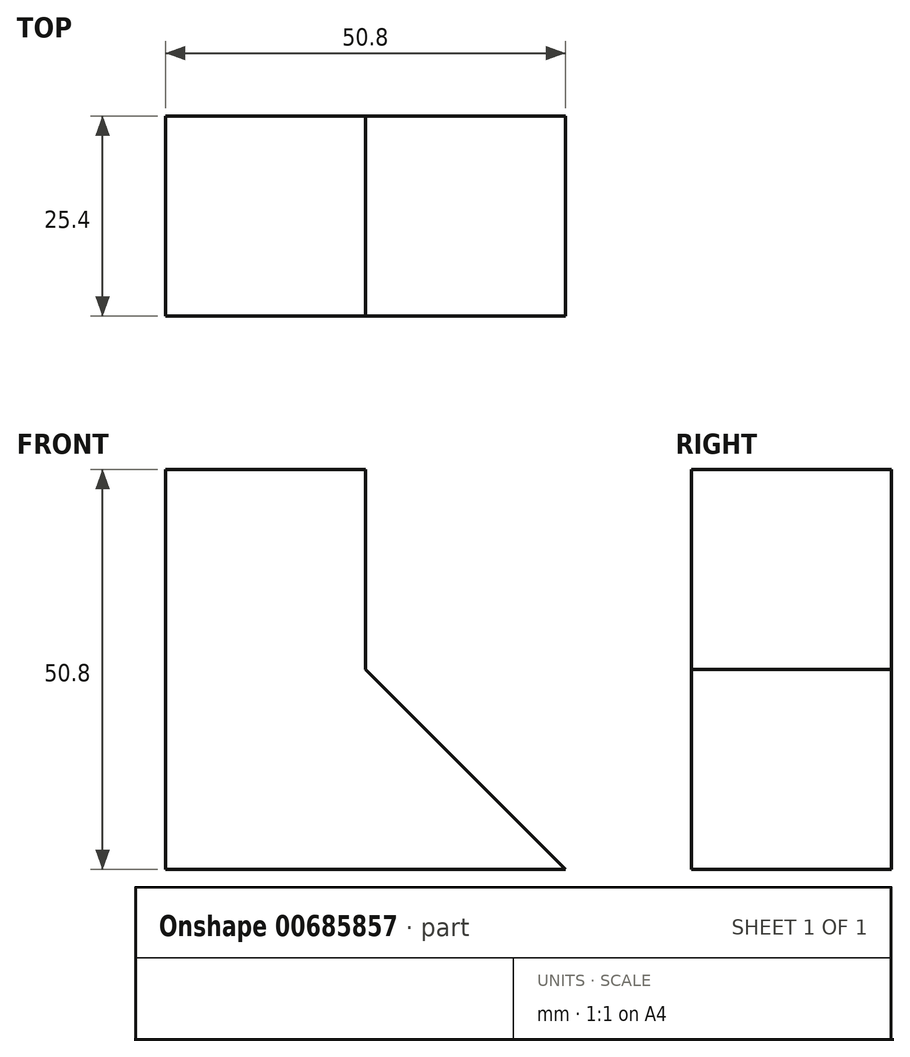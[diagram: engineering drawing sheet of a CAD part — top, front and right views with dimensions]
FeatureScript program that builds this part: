
annotation { "Feature Type Name" : "Feature", "Feature Type Description" : "" }
export const myFeature = defineFeature(function(context is Context, id is Id, definition is map)
    precondition{}
    {
        {
            var Q0;
            Q0=qCreatedBy(makeId("Front.planeOp"),FACE);
            var sketch = newSketch(context, id + "F0", { "sketchPlane" : qUnion([Q0])});
            skLineSegment(sketch, "E0", {"start": v(-25.4, 20.15) * mm, "end": v(-25.4, -30.65) * mm});
            skLineSegment(sketch, "E1", {"start": v(-25.4, 20.15) * mm, "end": v(0, 20.15) * mm});
            skLineSegment(sketch, "E2", {"start": v(0, 20.15) * mm, "end": v(0, -5.25) * mm});
            skLineSegment(sketch, "E3", {"start": v(-25.4, -30.65) * mm, "end": v(25.4, -30.65) * mm});
            skLineSegment(sketch, "E4", {"start": v(0, -5.25) * mm, "end": v(25.4, -30.65) * mm});
            skSolve(sketch);
        }
        {
            var Q0;
            Q0=makeQuery(id+"F0.imprint","IMPRINT",FACE,{"disambiguationData":[TD([[makeQuery(id+"F0.imprint","IMPRINT",EDGE,{"derivedFrom":sQuery(id+"F0.wireOp",EDGE,"E0")}),1.0]])]});
            extrude(context, id + "F1", {"entities" : qUnion([Q0]), "depth" : 25.4 * mm, "offsetDistance" : 25.4 * mm});
        }
    });
